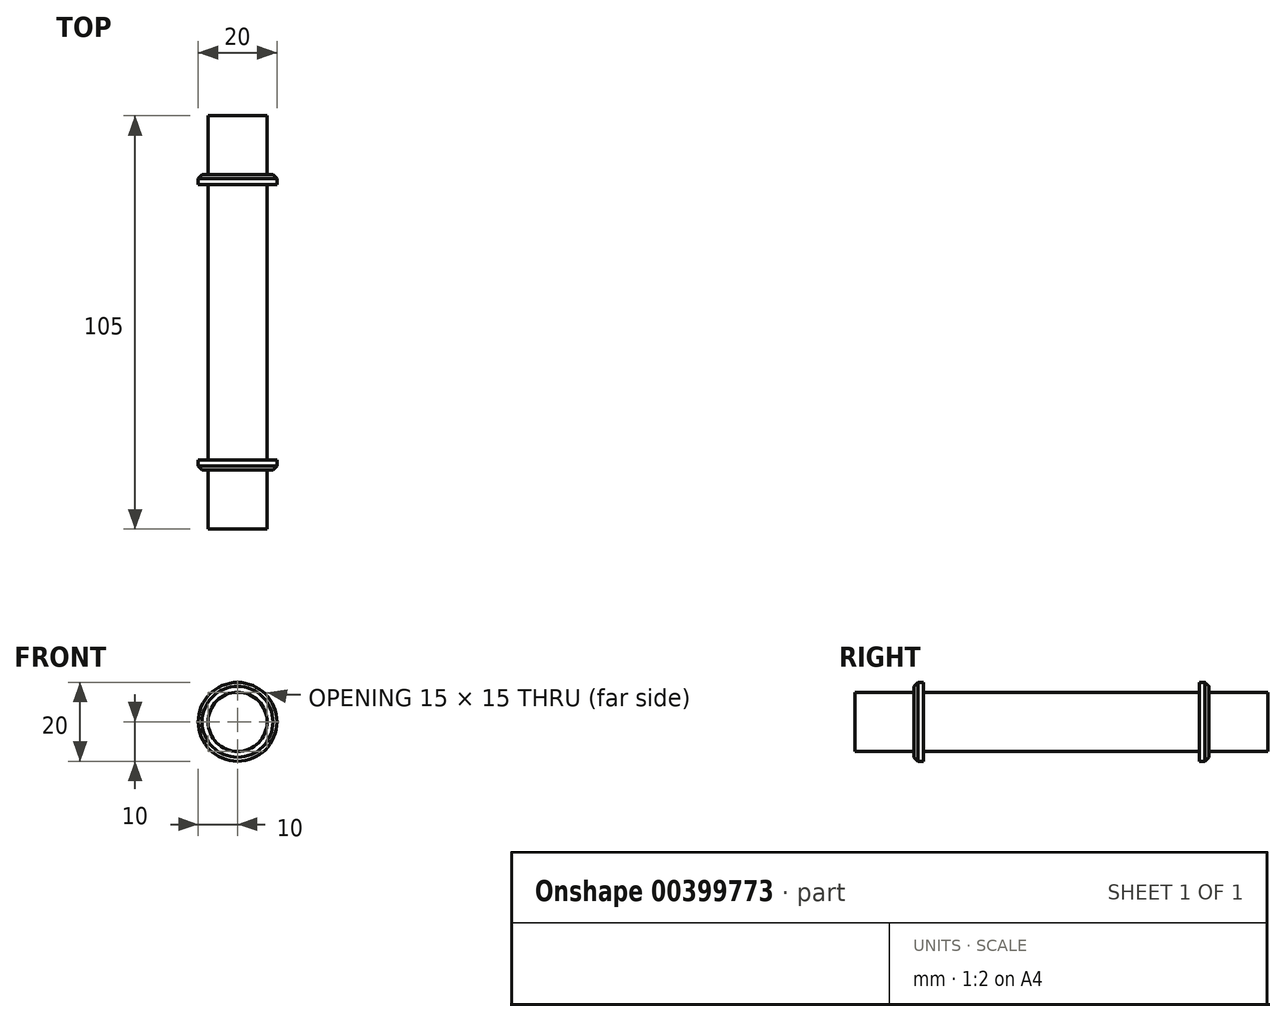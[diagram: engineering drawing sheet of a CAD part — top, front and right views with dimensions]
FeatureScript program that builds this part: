
annotation { "Feature Type Name" : "Feature", "Feature Type Description" : "" }
export const myFeature = defineFeature(function(context is Context, id is Id, definition is map)
    precondition{}
    {
        {
            var Q0;
            Q0=qCreatedBy(makeId("Front.planeOp"),FACE);
            var sketch = newSketch(context, id + "F0", { "sketchPlane" : qUnion([Q0])});
            skCircle(sketch, "E0", {"center": v(0, 0) * mm, "radius": 7.5 * mm});
            skSolve(sketch);
        }
        {
            var Q0;
            Q0 = qSketchRegion(id + "F0", true);
            extrude(context, id + "F1", {"entities" : qUnion([Q0]), "oppositeDirection" : true, "depth" : 105 * mm});
        }
        {
            var Q0;
            Q0=qCreatedBy(makeId("Front.planeOp"),FACE);
            cPlane(context, id + "F2", {"entities" : qUnion([Q0]), "cplaneType" : CPlaneType.OFFSET, "offset" : 15 * mm, "oppositeDirection" : true, "width" : 152.4 * mm, "height" : 152.4 * mm});
        }
        {
            var Q0;
            Q0=qCreatedBy(id+"F2.planeOp",FACE);
            var sketch = newSketch(context, id + "F3", { "sketchPlane" : qUnion([Q0])});
            skCircle(sketch, "E1", {"center": v(0, 0) * mm, "radius": 10 * mm});
            skSolve(sketch);
        }
        {
            var Q0;
            Q0 = qSketchRegion(id + "F3", true);
            extrude(context, id + "F4", {"entities" : qUnion([Q0]), "operationType" : NewBodyOperationType.ADD, "oppositeDirection" : true, "depth" : 2.5 * mm});
        }
        {
            var Q0;
            Q0=makeQuery(id+"F1.opExtrude","CAP_FACE",FACE,{"disambiguationData":[OSD([sQuery(id+"F0.wireOp",EDGE,"E0")])],"isStart":false});
            cPlane(context, id + "F5", {"entities" : qUnion([Q0]), "cplaneType" : CPlaneType.OFFSET, "offset" : 15 * mm, "oppositeDirection" : true, "width" : 152.4 * mm, "height" : 152.4 * mm});
        }
        {
            var Q0;
            Q0=qCreatedBy(id+"F5.planeOp",FACE);
            var sketch = newSketch(context, id + "F6", { "sketchPlane" : qUnion([Q0])});
            skCircle(sketch, "E2.0", {"center": v(0, 0) * mm, "radius": 10 * mm});
            skSolve(sketch);
        }
        {
            var Q0;
            Q0 = qSketchRegion(id + "F6", true);
            extrude(context, id + "F7", {"entities" : qUnion([Q0]), "operationType" : NewBodyOperationType.ADD, "oppositeDirection" : true, "depth" : 2.5 * mm});
        }
        {
            var Q0;
            Q0=makeQuery(id+"F4.opExtrude","CAP_EDGE",EDGE,{"disambiguationData":[OSD([sQuery(id+"F3.wireOp",EDGE,"E1")])],"isStart":true});
            var Q1;
            Q1=makeQuery(id+"F7.opExtrude","CAP_EDGE",EDGE,{"disambiguationData":[OSD([sQuery(id+"F6.wireOp",EDGE,"E2.0")])],"isStart":true});
            chamfer(context, id + "F8", {"entities" : qUnion([Q0, Q1]), "width" : 1 * mm, "tangentPropagation" : true});
        }
    });
